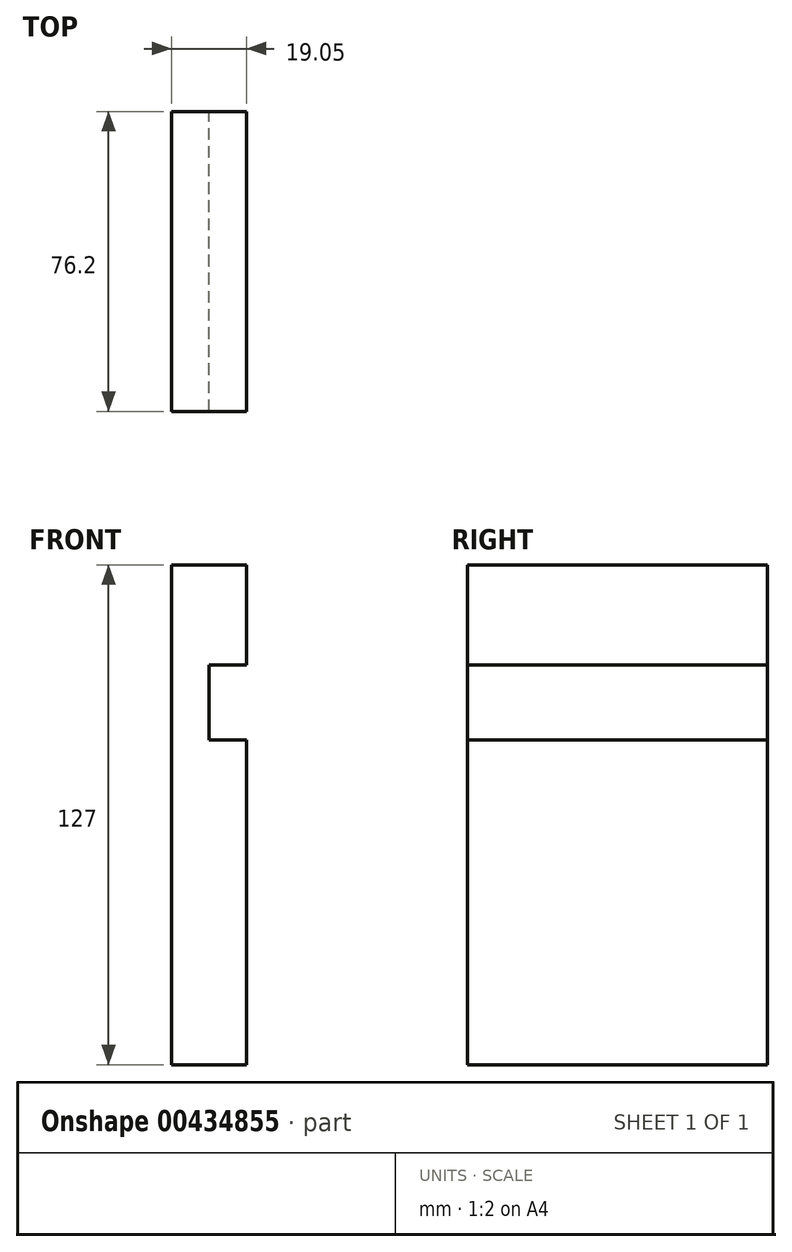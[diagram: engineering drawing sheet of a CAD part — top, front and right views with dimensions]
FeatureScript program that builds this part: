
annotation { "Feature Type Name" : "Feature", "Feature Type Description" : "" }
export const myFeature = defineFeature(function(context is Context, id is Id, definition is map)
    precondition{}
    {
        {
            var Q0;
            Q0=qCreatedBy(makeId("Front.planeOp"),FACE);
            var sketch = newSketch(context, id + "F0", { "sketchPlane" : qUnion([Q0])});
            skLineSegment(sketch, "E0", {"start": v(0, 60.49) * mm, "end": v(0, -66.51) * mm});
            skLineSegment(sketch, "E1", {"start": v(0, -66.51) * mm, "end": v(19.05, -66.51) * mm});
            skLineSegment(sketch, "E2", {"start": v(19.05, -66.51) * mm, "end": v(19.05, 16.04) * mm});
            skLineSegment(sketch, "E3", {"start": v(19.05, 16.04) * mm, "end": v(9.53, 16.04) * mm});
            skLineSegment(sketch, "E4", {"start": v(9.53, 16.04) * mm, "end": v(9.53, 35.09) * mm});
            skLineSegment(sketch, "E5", {"start": v(9.53, 35.09) * mm, "end": v(19.05, 35.09) * mm});
            skLineSegment(sketch, "E6", {"start": v(19.05, 35.09) * mm, "end": v(19.05, 60.49) * mm});
            skLineSegment(sketch, "E7", {"start": v(19.05, 60.49) * mm, "end": v(0, 60.49) * mm});
            skSolve(sketch);
        }
        {
            var Q0;
            Q0 = qSketchRegion(id + "F0", true);
            extrude(context, id + "F1", {"entities" : qUnion([Q0]), "depth" : 76.2 * mm});
        }
    });
